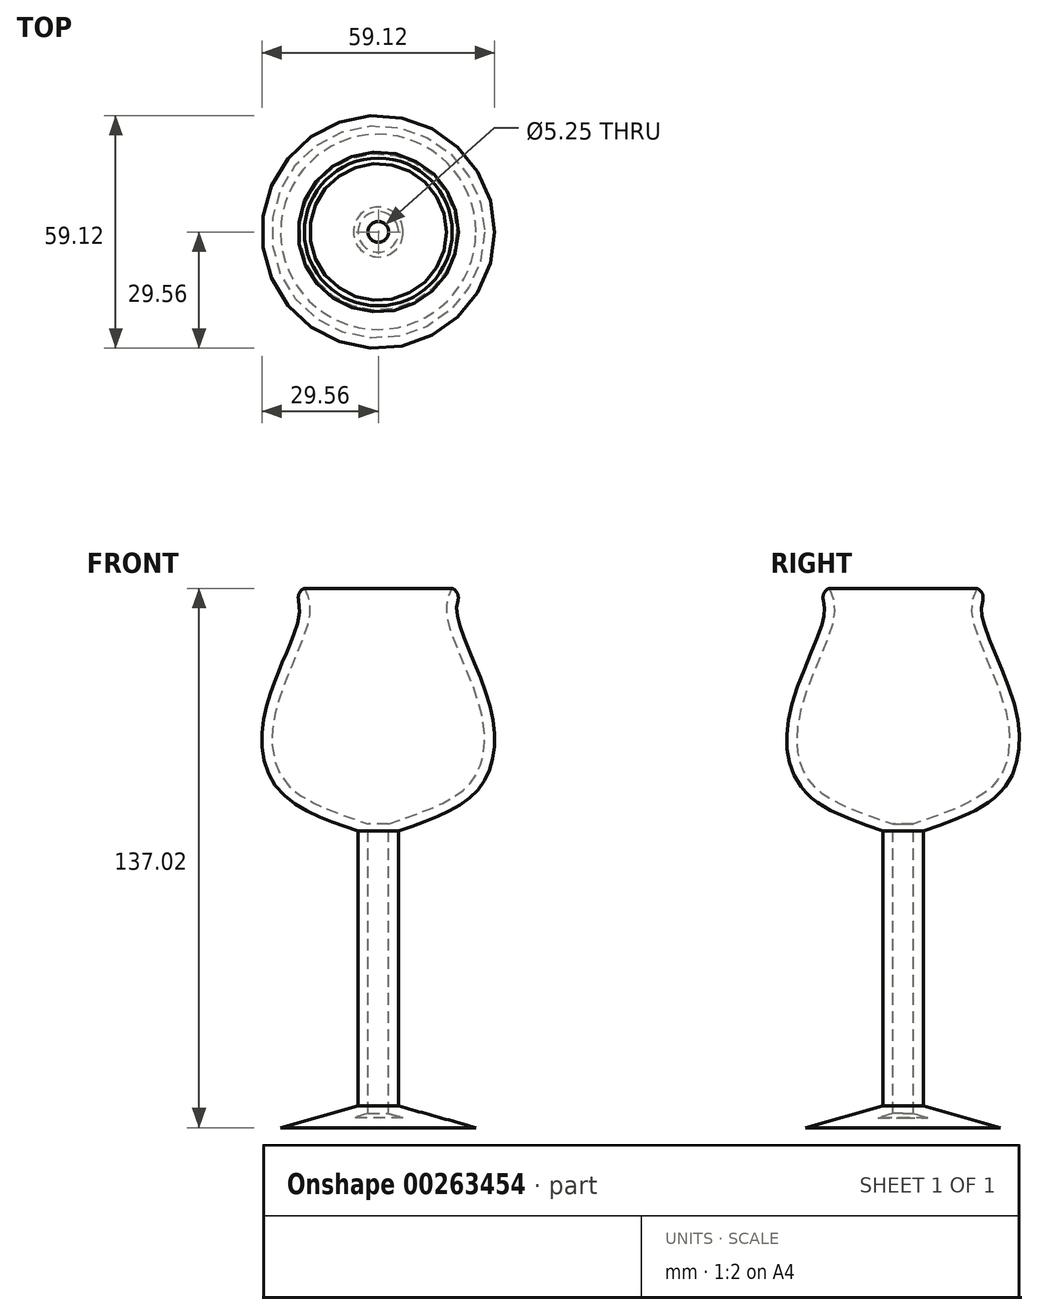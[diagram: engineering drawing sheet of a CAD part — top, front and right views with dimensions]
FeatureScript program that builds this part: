
annotation { "Feature Type Name" : "Feature", "Feature Type Description" : "" }
export const myFeature = defineFeature(function(context is Context, id is Id, definition is map)
    precondition{}
    {
        {
            var Q0;
            Q0=qCreatedBy(makeId("Front.planeOp"),FACE);
            var sketch = newSketch(context, id + "F0", { "sketchPlane" : qUnion([Q0])});
            skLineSegment(sketch, "E0", {"start": v(0, -75.4) * mm, "end": v(-24.79, -75.4) * mm});
            skLineSegment(sketch, "E1", {"start": v(-24.79, -75.4) * mm, "end": v(-5.16, -69.89) * mm});
            skLineSegment(sketch, "E2", {"start": v(-5.16, -69.89) * mm, "end": v(-5.16, 0) * mm});
            skFitSpline(sketch, "E3", {"points": [v(-5.16, 0) * mm, v(-25.48, 10.67) * mm, v(-28.57, 30.98) * mm, v(-19.97, 55.43) * mm, v(-21.69, 61.62) * mm], "startDerivative": vector(-84.6, 28.63) * mm, "endDerivative": vector(-20.19, 34.28) * mm});
            skLineSegment(sketch, "E4", {"start": v(-21.69, 61.62) * mm, "end": v(0, 61.62) * mm});
            skLineSegment(sketch, "E5", {"start": v(0, 61.62) * mm, "end": v(0, -75.4) * mm});
            skSolve(sketch);
        }
        {
            var Q0;
            Q0=makeQuery(id+"F0.imprint","IMPRINT",FACE,{"disambiguationData":[TD([[makeQuery(id+"F0.imprint","IMPRINT",EDGE,{"derivedFrom":sQuery(id+"F0.wireOp",EDGE,"E0")}),-1.0]])]});
            var Q1;
            Q1=sQuery(id+"F0.wireOp",EDGE,"E5");
            revolve(context, id + "F1", {"entities" : qUnion([Q0]), "axis" : qUnion([Q1]), "revolveType" : RevolveType.FULL});
        }
        {
            var Q0;
            Q0=makeQuery(id+"F1.opRevolve","SWEPT_FACE",FACE,{"disambiguationData":[OSD([sQuery(id+"F0.wireOp",EDGE,"E4")])]});
            shell(context, id + "F2", {"entities" : qUnion([Q0]), "thickness" : 2.54 * mm});
        }
        {
            var Q0;
            Q0=makeQuery(id+"F1.opRevolve","SWEPT_EDGE",EDGE,{"disambiguationData":[OSD([sQuery(id+"F0.wireOp",EDGE,"E3"),sQuery(id+"F0.wireOp",EDGE,"E4")])]});
            fillet(context, id + "F3", {"entities" : qUnion([Q0]), "radius" : 2.54 * mm, "tangentPropagation" : true, "allowEdgeOverflow" : false});
        }
    });
